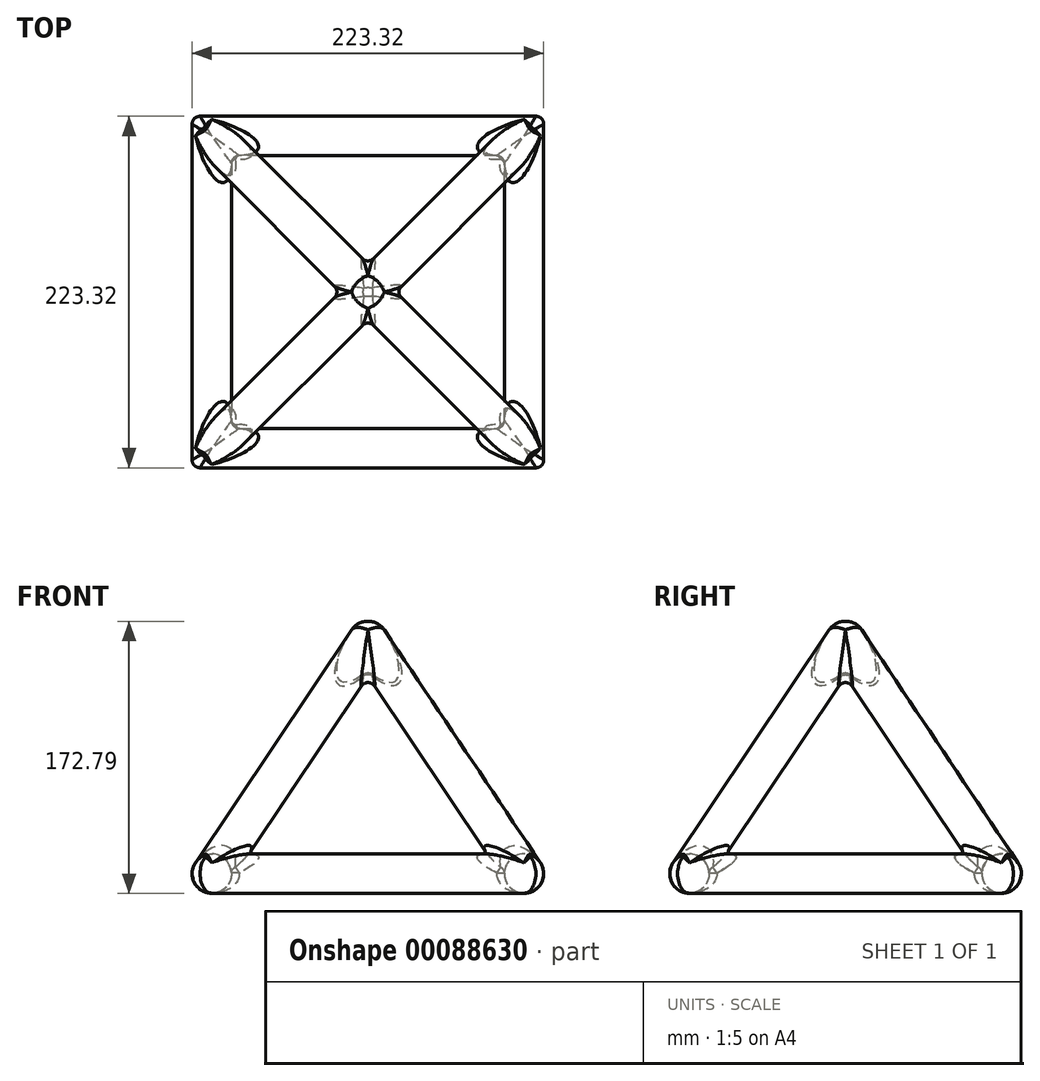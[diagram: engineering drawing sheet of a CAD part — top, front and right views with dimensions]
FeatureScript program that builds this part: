
annotation { "Feature Type Name" : "Feature", "Feature Type Description" : "" }
export const myFeature = defineFeature(function(context is Context, id is Id, definition is map)
    precondition{}
    {
        {
            var Q0;
            Q0=qCreatedBy(makeId("Top.planeOp"),FACE);
            var sketch = newSketch(context, id + "F0", { "sketchPlane" : qUnion([Q0])});
            skLineSegment(sketch, "E0.bottom", {"start": v(99.16, -99.16) * mm, "end": v(-99.16, -99.16) * mm});
            skLineSegment(sketch, "E0.top", {"start": v(99.16, 99.16) * mm, "end": v(-99.16, 99.16) * mm});
            skLineSegment(sketch, "E0.left", {"start": v(99.16, -99.16) * mm, "end": v(99.16, 99.16) * mm});
            skLineSegment(sketch, "E0.right", {"start": v(-99.16, -99.16) * mm, "end": v(-99.16, 99.16) * mm});
            skPoint(sketch, "E0.middle", {"position": v(0, 0) * mm});
            skSolve(sketch);
        }
        {
            var Q0;
            Q0=qCreatedBy(makeId("Right.planeOp"),FACE);
            var sketch = newSketch(context, id + "F1", { "sketchPlane" : qUnion([Q0])});
            skLineSegment(sketch, "E1", {"start": v(0, 0) * mm, "end": v(0, 147.79) * mm, "construction": true});
            skSolve(sketch);
        }
        {
            var Q0;
            Q0=sQuery(id+"F1.wireOp",VERTEX,"E1.end");
            var Q1;
            Q1=sQuery(id+"F0.wireOp",VERTEX,"E0.right.start");
            var Q2;
            Q2=sQuery(id+"F0.wireOp",VERTEX,"E0.bottom.start");
            cPlane(context, id + "F2", {"entities" : qUnion([Q0, Q1, Q2]), "cplaneType" : CPlaneType.THREE_POINT, "offset" : 150 * mm, "width" : 150 * mm, "height" : 150 * mm});
        }
        {
            var Q0;
            Q0=sQuery(id+"F0.wireOp",EDGE,"E0.left");
            var Q1;
            Q1=sQuery(id+"F0.wireOp",VERTEX,"E0.bottom.start");
            cPlane(context, id + "F3", {"entities" : qUnion([Q0, Q1]), "cplaneType" : CPlaneType.LINE_POINT, "offset" : 150 * mm, "width" : 150 * mm, "height" : 150 * mm});
        }
        {
            var Q0;
            Q0=qCreatedBy(id+"F3.planeOp",FACE);
            var sketch = newSketch(context, id + "F4", { "sketchPlane" : qUnion([Q0])});
            skCircle(sketch, "E2", {"center": v(-99.16, 0) * mm, "radius": 12.5 * mm});
            skSolve(sketch);
        }
        {
            var Q0;
            Q0=makeQuery(id+"F4.imprint","IMPRINT",FACE,{"disambiguationData":[TD([[makeQuery(id+"F4.imprint","IMPRINT",EDGE,{"derivedFrom":sQuery(id+"F4.wireOp",EDGE,"E2")}),1.0]])]});
            var Q1;
            Q1=sQuery(id+"F0.wireOp",EDGE,"E0.left");
            var Q2;
            Q2=sQuery(id+"F0.wireOp",EDGE,"E0.top");
            var Q3;
            Q3=sQuery(id+"F0.wireOp",EDGE,"E0.right");
            var Q4;
            Q4=sQuery(id+"F0.wireOp",EDGE,"E0.bottom");
            sweep(context, id + "F5", {"profiles" : qUnion([Q0]), "path" : qUnion([Q1, Q2, Q3, Q4])});
        }
        {
            var Q0;
            Q0=qCreatedBy(id+"F2.planeOp",FACE);
            var sketch = newSketch(context, id + "F6", { "sketchPlane" : qUnion([Q0])});
            skLineSegment(sketch, "E3", {"start": v(0, 122.72) * mm, "end": v(-99.16, -55.25) * mm});
            skSolve(sketch);
        }
        {
            var Q0;
            Q0=sQuery(id+"F6.wireOp",EDGE,"E3");
            var Q1;
            Q1=sQuery(id+"F6.wireOp",VERTEX,"E3.end");
            cPlane(context, id + "F7", {"entities" : qUnion([Q0, Q1]), "cplaneType" : CPlaneType.LINE_POINT, "offset" : 150 * mm, "width" : 150 * mm, "height" : 150 * mm});
        }
        {
            var Q0;
            Q0=qCreatedBy(id+"F7.planeOp",FACE);
            var sketch = newSketch(context, id + "F8", { "sketchPlane" : qUnion([Q0])});
            skCircle(sketch, "E4", {"center": v(59.73, 82.34) * mm, "radius": 12.5 * mm});
            skSolve(sketch);
        }
        {
            var Q0;
            Q0=makeQuery(id+"F8.imprint","IMPRINT",FACE,{"disambiguationData":[TD([[makeQuery(id+"F8.imprint","IMPRINT",EDGE,{"derivedFrom":sQuery(id+"F8.wireOp",EDGE,"E4")}),1.0]])]});
            var Q1;
            Q1=sQuery(id+"F6.wireOp",EDGE,"E3");
            sweep(context, id + "F9", {"profiles" : qUnion([Q0]), "path" : qUnion([Q1])});
        }
        {
            var Q0;
            Q0=makeQuery(id+"F9.opSweep","SWEPT_BODY",BODY,{"disambiguationData":[OSD([sQuery(id+"F6.wireOp",EDGE,"E3"),sQuery(id+"F8.wireOp",EDGE,"E4")])]});
            var Q1;
            Q1=sQuery(id+"F1.wireOp",EDGE,"E1");
            circularPattern(context, id + "F10", {"entities" : qUnion([Q0]), "axis" : qUnion([Q1]), "angle" : 360 * degree, "instanceCount" : 4, "equalSpace" : true, "computeTransformsWithoutBuiltin" : true});
        }
        {
            var Q0;
            Q0=qCreatedBy(makeId("Front.planeOp"),FACE);
            var sketch = newSketch(context, id + "F11", { "sketchPlane" : qUnion([Q0])});
            skLineSegment(sketch, "E5", {"start": v(-12.5, 147.79) * mm, "end": v(12.5, 147.79) * mm});
            skArc(sketch, "E6", {"start": v(12.5, 147.79) * mm, "mid": v(0, 160.29) * mm, "end": v(-12.5, 147.79) * mm});
            skSolve(sketch);
        }
        {
            var Q0;
            Q0 = qSketchRegion(id + "F11", true);
            var Q1;
            Q1=sQuery(id+"F11.wireOp",EDGE,"E5");
            revolve(context, id + "F12", {"entities" : qUnion([Q0]), "axis" : qUnion([Q1]), "revolveType" : RevolveType.FULL});
        }
        {
            var Q0;
            Q0=makeQuery(id+"F5.opSweep","SWEPT_BODY",BODY,{"disambiguationData":[OSD([sQuery(id+"F0.wireOp",EDGE,"E0.bottom"),sQuery(id+"F4.wireOp",EDGE,"E2")])]});
            var Q1;
            Q1=makeQuery(id+"F9.opSweep","SWEPT_BODY",BODY,{"disambiguationData":[OSD([sQuery(id+"F6.wireOp",EDGE,"E3"),sQuery(id+"F8.wireOp",EDGE,"E4")])]});
            var Q2;
            Q2=makeQuery(id+"F10.opPattern","COPY",BODY,{"derivedFrom":makeQuery(id+"F9.opSweep","SWEPT_BODY",BODY,{"disambiguationData":[OSD([sQuery(id+"F6.wireOp",EDGE,"E3"),sQuery(id+"F8.wireOp",EDGE,"E4")])]}),"instanceName":"1"});
            var Q3;
            Q3=makeQuery(id+"F10.opPattern","COPY",BODY,{"derivedFrom":makeQuery(id+"F9.opSweep","SWEPT_BODY",BODY,{"disambiguationData":[OSD([sQuery(id+"F6.wireOp",EDGE,"E3"),sQuery(id+"F8.wireOp",EDGE,"E4")])]}),"instanceName":"2"});
            var Q4;
            Q4=makeQuery(id+"F10.opPattern","COPY",BODY,{"derivedFrom":makeQuery(id+"F9.opSweep","SWEPT_BODY",BODY,{"disambiguationData":[OSD([sQuery(id+"F6.wireOp",EDGE,"E3"),sQuery(id+"F8.wireOp",EDGE,"E4")])]}),"instanceName":"3"});
            var Q5;
            Q5=makeQuery(id+"F12.opRevolve","SWEPT_BODY",BODY,{"disambiguationData":[OSD([sQuery(id+"F11.wireOp",EDGE,"E5"),sQuery(id+"F11.wireOp",EDGE,"E6")])]});
            booleanBodies(context, id + "F13", {"operationType" : BooleanOperationType.UNION, "tools" : qUnion([Q0, Q1, Q2, Q3, Q4, Q5])});
        }
        {
            var Q0;
            Q0=makeQuery(id+"F13.opBoolean","INTERSECT",EDGE,{"disambiguationData":[OD(0.0)],"derivedFrom":[makeQuery(id+"F5.opSweep","SWEPT_FACE",FACE,{"disambiguationData":[OSD([sQuery(id+"F0.wireOp",EDGE,"E0.left"),sQuery(id+"F4.wireOp",EDGE,"E2")])]}),makeQuery(id+"F9.opSweep","SWEPT_FACE",FACE,{"disambiguationData":[OSD([sQuery(id+"F6.wireOp",EDGE,"E3"),sQuery(id+"F8.wireOp",EDGE,"E4")])]})]});
            var Q1;
            Q1=makeQuery(id+"F13.opBoolean","INTERSECT",EDGE,{"disambiguationData":[OD(1.0)],"derivedFrom":[makeQuery(id+"F5.opSweep","SWEPT_FACE",FACE,{"disambiguationData":[OSD([sQuery(id+"F0.wireOp",EDGE,"E0.left"),sQuery(id+"F4.wireOp",EDGE,"E2")])]}),makeQuery(id+"F9.opSweep","SWEPT_FACE",FACE,{"disambiguationData":[OSD([sQuery(id+"F6.wireOp",EDGE,"E3"),sQuery(id+"F8.wireOp",EDGE,"E4")])]})]});
            var Q2;
            Q2=makeQuery(id+"F13.opBoolean","INTERSECT",EDGE,{"disambiguationData":[OD(1.0)],"derivedFrom":[makeQuery(id+"F5.opSweep","SWEPT_FACE",FACE,{"disambiguationData":[OSD([sQuery(id+"F0.wireOp",EDGE,"E0.bottom"),sQuery(id+"F4.wireOp",EDGE,"E2")])]}),makeQuery(id+"F9.opSweep","SWEPT_FACE",FACE,{"disambiguationData":[OSD([sQuery(id+"F6.wireOp",EDGE,"E3"),sQuery(id+"F8.wireOp",EDGE,"E4")])]})]});
            var Q3;
            Q3=makeQuery(id+"F5.opSweep","CAP_EDGE",EDGE,{"disambiguationData":[OSD([sQuery(id+"F0.wireOp",VERTEX,"E0.bottom.start"),sQuery(id+"F4.wireOp",EDGE,"E2")])],"isStart":true});
            var Q4;
            Q4=makeQuery(id+"F13.opBoolean","INTERSECT",EDGE,{"disambiguationData":[OD(0.0)],"derivedFrom":[makeQuery(id+"F5.opSweep","SWEPT_FACE",FACE,{"disambiguationData":[OSD([sQuery(id+"F0.wireOp",EDGE,"E0.bottom"),sQuery(id+"F4.wireOp",EDGE,"E2")])]}),makeQuery(id+"F9.opSweep","SWEPT_FACE",FACE,{"disambiguationData":[OSD([sQuery(id+"F6.wireOp",EDGE,"E3"),sQuery(id+"F8.wireOp",EDGE,"E4")])]})]});
            var Q5;
            Q5=makeQuery(id+"F5.opSweep","MID_CAP_EDGE",EDGE,{"disambiguationData":[OSD([sQuery(id+"F0.wireOp",VERTEX,"E0.top.start"),sQuery(id+"F4.wireOp",EDGE,"E2")])],"capPos":1.0});
            var Q6;
            Q6=makeQuery(id+"F13.opBoolean","INTERSECT",EDGE,{"disambiguationData":[OD(1.0)],"derivedFrom":[makeQuery(id+"F5.opSweep","SWEPT_FACE",FACE,{"disambiguationData":[OSD([sQuery(id+"F0.wireOp",EDGE,"E0.top"),sQuery(id+"F4.wireOp",EDGE,"E2")])]}),makeQuery(id+"F10.opPattern","COPY",FACE,{"derivedFrom":makeQuery(id+"F9.opSweep","SWEPT_FACE",FACE,{"disambiguationData":[OSD([sQuery(id+"F6.wireOp",EDGE,"E3"),sQuery(id+"F8.wireOp",EDGE,"E4")])]}),"instanceName":"1"})]});
            var Q7;
            Q7=makeQuery(id+"F13.opBoolean","INTERSECT",EDGE,{"disambiguationData":[OD(1.0)],"derivedFrom":[makeQuery(id+"F5.opSweep","SWEPT_FACE",FACE,{"disambiguationData":[OSD([sQuery(id+"F0.wireOp",EDGE,"E0.left"),sQuery(id+"F4.wireOp",EDGE,"E2")])]}),makeQuery(id+"F10.opPattern","COPY",FACE,{"derivedFrom":makeQuery(id+"F9.opSweep","SWEPT_FACE",FACE,{"disambiguationData":[OSD([sQuery(id+"F6.wireOp",EDGE,"E3"),sQuery(id+"F8.wireOp",EDGE,"E4")])]}),"instanceName":"1"})]});
            var Q8;
            Q8=makeQuery(id+"F13.opBoolean","INTERSECT",EDGE,{"disambiguationData":[OD(0.0)],"derivedFrom":[makeQuery(id+"F5.opSweep","SWEPT_FACE",FACE,{"disambiguationData":[OSD([sQuery(id+"F0.wireOp",EDGE,"E0.left"),sQuery(id+"F4.wireOp",EDGE,"E2")])]}),makeQuery(id+"F10.opPattern","COPY",FACE,{"derivedFrom":makeQuery(id+"F9.opSweep","SWEPT_FACE",FACE,{"disambiguationData":[OSD([sQuery(id+"F6.wireOp",EDGE,"E3"),sQuery(id+"F8.wireOp",EDGE,"E4")])]}),"instanceName":"1"})]});
            var Q9;
            Q9=makeQuery(id+"F13.opBoolean","INTERSECT",EDGE,{"disambiguationData":[OD(0.0)],"derivedFrom":[makeQuery(id+"F5.opSweep","SWEPT_FACE",FACE,{"disambiguationData":[OSD([sQuery(id+"F0.wireOp",EDGE,"E0.top"),sQuery(id+"F4.wireOp",EDGE,"E2")])]}),makeQuery(id+"F10.opPattern","COPY",FACE,{"derivedFrom":makeQuery(id+"F9.opSweep","SWEPT_FACE",FACE,{"disambiguationData":[OSD([sQuery(id+"F6.wireOp",EDGE,"E3"),sQuery(id+"F8.wireOp",EDGE,"E4")])]}),"instanceName":"1"})]});
            var Q10;
            Q10=makeQuery(id+"F13.opBoolean","INTERSECT",EDGE,{"disambiguationData":[OD(0.0)],"derivedFrom":[makeQuery(id+"F5.opSweep","SWEPT_FACE",FACE,{"disambiguationData":[OSD([sQuery(id+"F0.wireOp",EDGE,"E0.top"),sQuery(id+"F4.wireOp",EDGE,"E2")])]}),makeQuery(id+"F10.opPattern","COPY",FACE,{"derivedFrom":makeQuery(id+"F9.opSweep","SWEPT_FACE",FACE,{"disambiguationData":[OSD([sQuery(id+"F6.wireOp",EDGE,"E3"),sQuery(id+"F8.wireOp",EDGE,"E4")])]}),"instanceName":"2"})]});
            var Q11;
            Q11=makeQuery(id+"F13.opBoolean","INTERSECT",EDGE,{"disambiguationData":[OD(0.0)],"derivedFrom":[makeQuery(id+"F5.opSweep","SWEPT_FACE",FACE,{"disambiguationData":[OSD([sQuery(id+"F0.wireOp",EDGE,"E0.right"),sQuery(id+"F4.wireOp",EDGE,"E2")])]}),makeQuery(id+"F10.opPattern","COPY",FACE,{"derivedFrom":makeQuery(id+"F9.opSweep","SWEPT_FACE",FACE,{"disambiguationData":[OSD([sQuery(id+"F6.wireOp",EDGE,"E3"),sQuery(id+"F8.wireOp",EDGE,"E4")])]}),"instanceName":"2"})]});
            var Q12;
            Q12=makeQuery(id+"F5.opSweep","MID_CAP_EDGE",EDGE,{"disambiguationData":[OSD([sQuery(id+"F0.wireOp",VERTEX,"E0.right.end"),sQuery(id+"F4.wireOp",EDGE,"E2")])],"capPos":2.0});
            var Q13;
            Q13=makeQuery(id+"F13.opBoolean","INTERSECT",EDGE,{"disambiguationData":[OD(1.0)],"derivedFrom":[makeQuery(id+"F5.opSweep","SWEPT_FACE",FACE,{"disambiguationData":[OSD([sQuery(id+"F0.wireOp",EDGE,"E0.right"),sQuery(id+"F4.wireOp",EDGE,"E2")])]}),makeQuery(id+"F10.opPattern","COPY",FACE,{"derivedFrom":makeQuery(id+"F9.opSweep","SWEPT_FACE",FACE,{"disambiguationData":[OSD([sQuery(id+"F6.wireOp",EDGE,"E3"),sQuery(id+"F8.wireOp",EDGE,"E4")])]}),"instanceName":"2"})]});
            var Q14;
            Q14=makeQuery(id+"F13.opBoolean","INTERSECT",EDGE,{"disambiguationData":[OD(1.0)],"derivedFrom":[makeQuery(id+"F5.opSweep","SWEPT_FACE",FACE,{"disambiguationData":[OSD([sQuery(id+"F0.wireOp",EDGE,"E0.top"),sQuery(id+"F4.wireOp",EDGE,"E2")])]}),makeQuery(id+"F10.opPattern","COPY",FACE,{"derivedFrom":makeQuery(id+"F9.opSweep","SWEPT_FACE",FACE,{"disambiguationData":[OSD([sQuery(id+"F6.wireOp",EDGE,"E3"),sQuery(id+"F8.wireOp",EDGE,"E4")])]}),"instanceName":"2"})]});
            var Q15;
            Q15=makeQuery(id+"F13.opBoolean","INTERSECT",EDGE,{"disambiguationData":[OD(1.0)],"derivedFrom":[makeQuery(id+"F5.opSweep","SWEPT_FACE",FACE,{"disambiguationData":[OSD([sQuery(id+"F0.wireOp",EDGE,"E0.right"),sQuery(id+"F4.wireOp",EDGE,"E2")])]}),makeQuery(id+"F10.opPattern","COPY",FACE,{"derivedFrom":makeQuery(id+"F9.opSweep","SWEPT_FACE",FACE,{"disambiguationData":[OSD([sQuery(id+"F6.wireOp",EDGE,"E3"),sQuery(id+"F8.wireOp",EDGE,"E4")])]}),"instanceName":"3"})]});
            var Q16;
            Q16=makeQuery(id+"F13.opBoolean","INTERSECT",EDGE,{"disambiguationData":[OD(1.0)],"derivedFrom":[makeQuery(id+"F5.opSweep","SWEPT_FACE",FACE,{"disambiguationData":[OSD([sQuery(id+"F0.wireOp",EDGE,"E0.bottom"),sQuery(id+"F4.wireOp",EDGE,"E2")])]}),makeQuery(id+"F10.opPattern","COPY",FACE,{"derivedFrom":makeQuery(id+"F9.opSweep","SWEPT_FACE",FACE,{"disambiguationData":[OSD([sQuery(id+"F6.wireOp",EDGE,"E3"),sQuery(id+"F8.wireOp",EDGE,"E4")])]}),"instanceName":"3"})]});
            var Q17;
            Q17=makeQuery(id+"F13.opBoolean","INTERSECT",EDGE,{"disambiguationData":[OD(0.0)],"derivedFrom":[makeQuery(id+"F5.opSweep","SWEPT_FACE",FACE,{"disambiguationData":[OSD([sQuery(id+"F0.wireOp",EDGE,"E0.bottom"),sQuery(id+"F4.wireOp",EDGE,"E2")])]}),makeQuery(id+"F10.opPattern","COPY",FACE,{"derivedFrom":makeQuery(id+"F9.opSweep","SWEPT_FACE",FACE,{"disambiguationData":[OSD([sQuery(id+"F6.wireOp",EDGE,"E3"),sQuery(id+"F8.wireOp",EDGE,"E4")])]}),"instanceName":"3"})]});
            var Q18;
            Q18=makeQuery(id+"F13.opBoolean","INTERSECT",EDGE,{"disambiguationData":[OD(0.0)],"derivedFrom":[makeQuery(id+"F5.opSweep","SWEPT_FACE",FACE,{"disambiguationData":[OSD([sQuery(id+"F0.wireOp",EDGE,"E0.right"),sQuery(id+"F4.wireOp",EDGE,"E2")])]}),makeQuery(id+"F10.opPattern","COPY",FACE,{"derivedFrom":makeQuery(id+"F9.opSweep","SWEPT_FACE",FACE,{"disambiguationData":[OSD([sQuery(id+"F6.wireOp",EDGE,"E3"),sQuery(id+"F8.wireOp",EDGE,"E4")])]}),"instanceName":"3"})]});
            var Q19;
            Q19=makeQuery(id+"F5.opSweep","SWEPT_FACE",FACE,{"disambiguationData":[OSD([sQuery(id+"F0.wireOp",EDGE,"E0.right"),sQuery(id+"F4.wireOp",EDGE,"E2")])]});
            var Q20;
            {var subQ0=makeQuery(id+"F9.opSweep","SWEPT_FACE",FACE,{"disambiguationData":[OSD([sQuery(id+"F6.wireOp",EDGE,"E3"),sQuery(id+"F8.wireOp",EDGE,"E4")])]});Q20=makeQuery(id+"F13.opBoolean","INTERSECT",EDGE,{"derivedFrom":[subQ0,makeQuery(id+"F10.opPattern","COPY",FACE,{"derivedFrom":subQ0,"instanceName":"3"})]});}
            var Q21;
            {var subQ0=makeQuery(id+"F9.opSweep","SWEPT_FACE",FACE,{"disambiguationData":[OSD([sQuery(id+"F6.wireOp",EDGE,"E3"),sQuery(id+"F8.wireOp",EDGE,"E4")])]});Q21=makeQuery(id+"F13.opBoolean","INTERSECT",EDGE,{"derivedFrom":[makeQuery(id+"F10.opPattern","COPY",FACE,{"derivedFrom":subQ0,"instanceName":"2"}),makeQuery(id+"F10.opPattern","COPY",FACE,{"derivedFrom":subQ0,"instanceName":"3"})]});}
            var Q22;
            {var subQ0=makeQuery(id+"F9.opSweep","SWEPT_FACE",FACE,{"disambiguationData":[OSD([sQuery(id+"F6.wireOp",EDGE,"E3"),sQuery(id+"F8.wireOp",EDGE,"E4")])]});Q22=makeQuery(id+"F13.opBoolean","INTERSECT",EDGE,{"derivedFrom":[subQ0,makeQuery(id+"F10.opPattern","COPY",FACE,{"derivedFrom":subQ0,"instanceName":"1"})]});}
            var Q23;
            {var subQ0=makeQuery(id+"F9.opSweep","SWEPT_FACE",FACE,{"disambiguationData":[OSD([sQuery(id+"F6.wireOp",EDGE,"E3"),sQuery(id+"F8.wireOp",EDGE,"E4")])]});Q23=makeQuery(id+"F13.opBoolean","INTERSECT",EDGE,{"derivedFrom":[makeQuery(id+"F10.opPattern","COPY",FACE,{"derivedFrom":subQ0,"instanceName":"1"}),makeQuery(id+"F10.opPattern","COPY",FACE,{"derivedFrom":subQ0,"instanceName":"2"})]});}
            var Q24;
            Q24=makeQuery(id+"F9.opSweep","CAP_EDGE",EDGE,{"disambiguationData":[OSD([sQuery(id+"F6.wireOp",VERTEX,"E3.start"),sQuery(id+"F8.wireOp",EDGE,"E4")])],"isStart":false});
            var Q25;
            Q25=makeQuery(id+"F10.opPattern","COPY",EDGE,{"derivedFrom":makeQuery(id+"F9.opSweep","CAP_EDGE",EDGE,{"disambiguationData":[OSD([sQuery(id+"F6.wireOp",VERTEX,"E3.start"),sQuery(id+"F8.wireOp",EDGE,"E4")])],"isStart":false}),"instanceName":"3"});
            var Q26;
            Q26=makeQuery(id+"F10.opPattern","COPY",EDGE,{"derivedFrom":makeQuery(id+"F9.opSweep","CAP_EDGE",EDGE,{"disambiguationData":[OSD([sQuery(id+"F6.wireOp",VERTEX,"E3.start"),sQuery(id+"F8.wireOp",EDGE,"E4")])],"isStart":false}),"instanceName":"2"});
            var Q27;
            Q27=makeQuery(id+"F10.opPattern","COPY",EDGE,{"derivedFrom":makeQuery(id+"F9.opSweep","CAP_EDGE",EDGE,{"disambiguationData":[OSD([sQuery(id+"F6.wireOp",VERTEX,"E3.start"),sQuery(id+"F8.wireOp",EDGE,"E4")])],"isStart":false}),"instanceName":"1"});
            fillet(context, id + "F14", {"entities" : qUnion([Q0, Q1, Q2, Q3, Q4, Q5, Q6, Q7, Q8, Q9, Q10, Q11, Q12, Q13, Q14, Q15, Q16, Q17, Q18, Q19, Q20, Q21, Q22, Q23, Q24, Q25, Q26, Q27]), "radius" : 5 * mm, "tangentPropagation" : true, "allowEdgeOverflow" : false});
        }
    });
